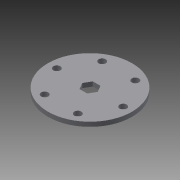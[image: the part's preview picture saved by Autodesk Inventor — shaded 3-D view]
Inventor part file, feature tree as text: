
AUTODESK INVENTOR PART (.ipt)
format: ipt  version: 2013 (Build 170138000, 138)  size: 94,208 bytes
history: native  units: in
note: dims shown in document units (in); Inventor stores cm internally (conversion verified against a paired STEP export)
features: extrude x1, sketch x1
ambient origin geometry x8: Origin, YZ Plane, XZ Plane, XY Plane, X Axis, Y Axis, Z Axis, Center Point
bodies: Solid1 (feature_tree)
feature tree (2):
  extrude  "Extrusion1"  Depth=0.2in
  sketch  "Sketch1"  dims[d0=0.2in d6=0.2in d8=0.2in d10=0.2in d11=2.375in d12=0.375in d13=0.125in d14=0.0in]
